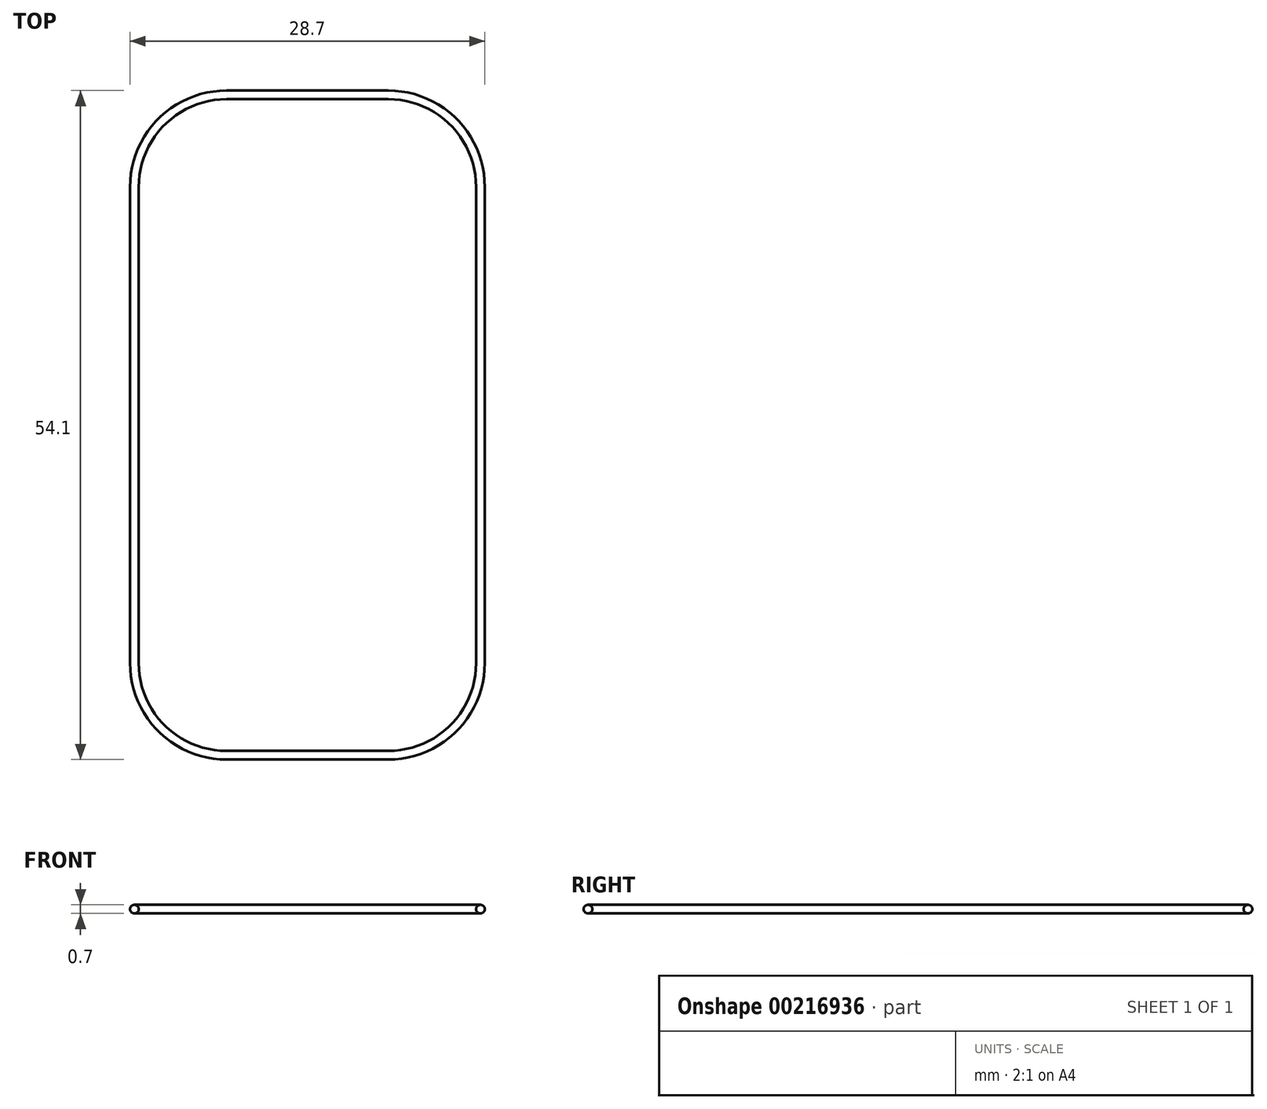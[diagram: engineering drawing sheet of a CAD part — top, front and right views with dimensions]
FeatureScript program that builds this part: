
annotation { "Feature Type Name" : "Feature", "Feature Type Description" : "" }
export const myFeature = defineFeature(function(context is Context, id is Id, definition is map)
    precondition{}
    {
        {
            var Q0;
            Q0=qCreatedBy(makeId("Top.planeOp"),FACE);
            var sketch = newSketch(context, id + "F0", { "sketchPlane" : qUnion([Q0])});
            skLineSegment(sketch, "E0.bottom", {"start": v(6.55, 26.2) * mm, "end": v(-6.55, 26.2) * mm, "construction": true});
            skLineSegment(sketch, "E0.top", {"start": v(6.55, -26.2) * mm, "end": v(-6.55, -26.2) * mm, "construction": true});
            skLineSegment(sketch, "E0.left", {"start": v(13.5, 19.25) * mm, "end": v(13.5, -19.25) * mm, "construction": true});
            skLineSegment(sketch, "E0.right", {"start": v(-13.5, 19.25) * mm, "end": v(-13.5, -19.25) * mm, "construction": true});
            skPoint(sketch, "E0.middle", {"position": v(0, 0) * mm});
            skPoint(sketch, "E1.visualSharp", {"position": v(-13.5, -26.2) * mm});
            skArc(sketch, "E1.filletArc", {"start": v(-13.5, -19.25) * mm, "mid": v(-11.46, -24.16) * mm, "end": v(-6.55, -26.2) * mm, "construction": true});
            skPoint(sketch, "E2.visualSharp", {"position": v(13.5, -26.2) * mm});
            skArc(sketch, "E2.filletArc", {"start": v(6.55, -26.2) * mm, "mid": v(11.46, -24.16) * mm, "end": v(13.5, -19.25) * mm, "construction": true});
            skPoint(sketch, "E3.visualSharp", {"position": v(13.5, 26.2) * mm});
            skArc(sketch, "E3.filletArc", {"start": v(13.5, 19.25) * mm, "mid": v(11.46, 24.16) * mm, "end": v(6.55, 26.2) * mm, "construction": true});
            skPoint(sketch, "E4.visualSharp", {"position": v(-13.5, 26.2) * mm});
            skArc(sketch, "E4.filletArc", {"start": v(-6.55, 26.2) * mm, "mid": v(-11.46, 24.16) * mm, "end": v(-13.5, 19.25) * mm, "construction": true});
            skLineSegment(sketch, "E5.0", {"start": v(6.55, 26.7) * mm, "end": v(-6.55, 26.7) * mm});
            skArc(sketch, "E5.1", {"start": v(14, 19.25) * mm, "mid": v(11.82, 24.52) * mm, "end": v(6.55, 26.7) * mm});
            skArc(sketch, "E5.2", {"start": v(-6.55, 26.7) * mm, "mid": v(-11.82, 24.52) * mm, "end": v(-14, 19.25) * mm});
            skLineSegment(sketch, "E5.3", {"start": v(14, 19.25) * mm, "end": v(14, -19.25) * mm});
            skLineSegment(sketch, "E5.4", {"start": v(-14, 19.25) * mm, "end": v(-14, -19.25) * mm});
            skArc(sketch, "E5.5", {"start": v(-14, -19.25) * mm, "mid": v(-11.82, -24.52) * mm, "end": v(-6.55, -26.7) * mm});
            skLineSegment(sketch, "E5.6", {"start": v(6.55, -26.7) * mm, "end": v(-6.55, -26.7) * mm});
            skArc(sketch, "E5.7", {"start": v(6.55, -26.7) * mm, "mid": v(11.82, -24.52) * mm, "end": v(14, -19.25) * mm});
            skLineSegment(sketch, "E6", {"start": v(-12.7, 13.6) * mm, "end": v(-12.7, -19.25) * mm, "construction": true});
            skLineSegment(sketch, "E7", {"start": v(-6.55, -25.4) * mm, "end": v(3.14, -25.4) * mm, "construction": true});
            skArc(sketch, "E8", {"start": v(-12.7, -19.25) * mm, "mid": v(-10.9, -23.6) * mm, "end": v(-6.55, -25.4) * mm, "construction": true});
            skSolve(sketch);
        }
        {
            var Q0;
            Q0=qCreatedBy(makeId("Front.planeOp"),FACE);
            var Q1;
            Q1=sQuery(id+"F0.wireOp",VERTEX,"E5.4.end");
            cPlane(context, id + "F1", {"entities" : qUnion([Q0, Q1]), "cplaneType" : CPlaneType.PLANE_POINT, "offset" : 25 * mm, "width" : 150 * mm, "height" : 150 * mm});
        }
        {
            var Q0;
            Q0=qCreatedBy(id+"F1.planeOp",FACE);
            var sketch = newSketch(context, id + "F2", { "sketchPlane" : qUnion([Q0])});
            skCircle(sketch, "E9", {"center": v(-14, 0) * mm, "radius": 0.35 * mm});
            skSolve(sketch);
        }
        {
            var Q0;
            Q0 = qSketchRegion(id + "F2", true);
            var Q1;
            Q1 = qConstructionFilter(qBodyType(qCreatedBy(id + "F0" ,EDGE), BodyType.WIRE), ConstructionObject.NO);
            sweep(context, id + "F3", {"profiles" : qUnion([Q0]), "path" : qUnion([Q1])});
        }
    });
